# Revit family: QF_T&S_B-0133
name_source: partatom
category: Specialty Equipment
revit_build: Autodesk Revit Architecture 2012 (Build: 20110916_2132(x64)
units: mm (PartAtom-declared; Revit-internal decimal feet)

## types (1)
- QF_T&S_B-0133
    Cold Water Connection Height = 0"
    Cold Water Inlet Flow = 1.420 GPM
    Cold Water Maximum Pressure = 125.00 psi
    Cold Water Minimum Pressure = 20.00 psi
    Cold Water Size = 1"
    Connector 1 Description = Cold Water Inlet
    Connector 2 Description = Hot Water Inlet
    Description = 8” wall mount mixing faucet with polished chrome plated brass body, 18'' riser, 44” flexible stainless steel hose with heat resistant handle, 1.42 GPM spray valve, compression cartridges with spring checks, lever handles, 1/2'' NPT female inlets, spray valve holder, and overhead spring.
    Faucet Material = Metal-T&S Brass-Stainless Steel
    Foodservice Equipment Identifier = Yes
    Hot Water Connection Height = 0"
    Hot Water Consumption = 1.420 GPM
    Hot Water Inlet Flow = 1.420 GPM
    Hot Water Maximum Pressure = 125.00 psi
    Hot Water Minimum Pressure = 20.00 psi
    Hot Water Size = 1"
    Identify Quantity as Lot = Yes
    Manufacturer = T&S Brass and Bronze Works, Inc.
    Manufacturer Fax = 1-800-868-0084
    Model = B-0133
    Plumbing Remarks = Pressure: 20 - 125 psi, Temperature: 40 F - 140 F, Flow Rate: 1.42 GPM @ 60 psi
    Product Documentation Link = http://catalog.tsbrass.com
    Product Page URL = http://www.tsbrass.com
    URL = http://www.tsbrass.com
    Water Supply Radius = 1/4"
    Weight in Pounds = 0

## geometry (parser evidence)
native form markers: Blend x6, Sweep x19
no freeform markers — native parametric forms only
